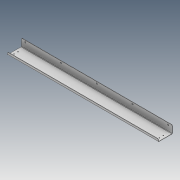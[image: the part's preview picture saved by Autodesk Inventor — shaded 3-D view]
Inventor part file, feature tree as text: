
AUTODESK INVENTOR PART (.ipt)
format: ipt  version: 2020 (Build 240168000, 168)  size: 164,864 bytes
history: native  units: mm
features: sheet_metal_op x7, sketch x5, other x4, hole x3, projected_geometry x3, fillet x1
ambient origin geometry x8: Origin, YZ Plane, XZ Plane, XY Plane, X Axis, Y Axis, Z Axis, Center Point
bodies: Solid1 (feature_tree)
feature tree (23):
  sheet_metal_op  "Face1"
  sheet_metal_op  "Flange1"
  sheet_metal_op  "Flange2"
  hole  "穴1"  [1 undecoded]
  fillet  "フィレット1"  Radius=1.5mm
  hole  "穴2"  [1 undecoded]
  other  "作業平面1"
  hole  "Hole3"  [1 undecoded]
  sketch  "Sketch1"  dims[d0=580.0mm d1=30.0mm d2=1.5mm]
  other  "Plate1"
  sketch  "Sketch2"  dims[d3=1.5mm d4=0.75mm]
  other  "Plate2"
  sheet_metal_op  "Bend1"
  sheet_metal_op  "Corner1"
  sketch  "Sketch3"  dims[d5=3.0mm d6=1.5mm]
  other  "Plate3"
  sheet_metal_op  "Bend2"
  sheet_metal_op  "Corner2"
  projected_geometry  "投影ループ1"
  sketch  "スケッチ5"
  projected_geometry  "投影ループ2"
  sketch  "Sketch7"  dims[d7=55.0mm d8=90.0deg d9=1.5mm d10=6.0mm d11=1.5mm d12=1.5mm d13=1.5mm d14=0.75mm d15=3.0mm d16=1.5mm d17=10.0mm d18=90.0deg d19=1.5mm d20=6.0mm d21=1.5mm d22=1.5mm d24=15.0mm d25=15.0mm d27=137.5mm d28=5.2mm d29=6.0mm d30=6.0mm d31=2.0mm d32=90.0deg d33=1.5mm d34=20.594885mm d35=3.0mm d36=15.0mm d40=10.0mm d41=3.242mm d42=8.0mm d43=6.0mm d44=2.0mm d45=90.0deg d46=11.8mm d47=20.594885mm d48=-335.0mm d50=10.0mm d51=3.242mm d52=8.0mm d53=4.0mm d54=2.0mm d55=90.0deg d56=11.8mm d57=20.594885mm d58=137.5mm d59=275.0mm d60=7.5mm d61=19.5mm]
  projected_geometry  "Projected Loop4"
note: 3 required parameter values undecoded (feature->parameter linkage not recoverable at this tier; creation-order binding heuristic only, values carry confidence <= 0.55)
